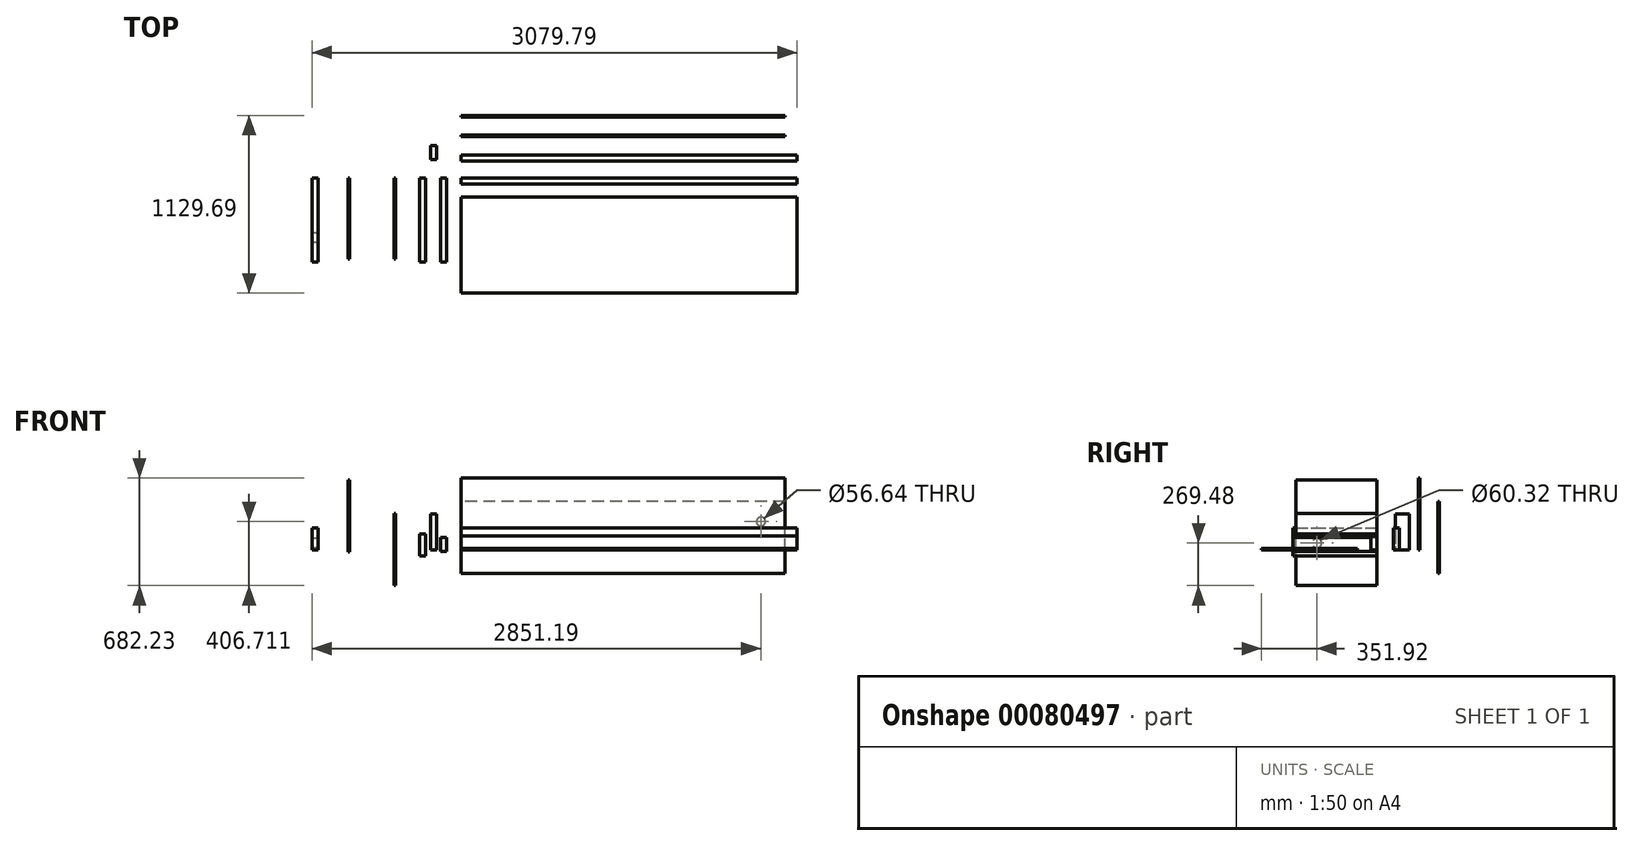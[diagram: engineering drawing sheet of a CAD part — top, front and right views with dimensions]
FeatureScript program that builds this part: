
annotation { "Feature Type Name" : "Feature", "Feature Type Description" : "" }
export const myFeature = defineFeature(function(context is Context, id is Id, definition is map)
    precondition{}
    {
        {
            var Q0;
            Q0=qCreatedBy(makeId("Right.planeOp"),FACE);
            var sketch = newSketch(context, id + "F0", { "sketchPlane" : qUnion([Q0])});
            skLineSegment(sketch, "E0.bottom", {"start": v(0, 0) * mm, "end": v(-38.1, 0) * mm});
            skLineSegment(sketch, "E0.top", {"start": v(0, 88.9) * mm, "end": v(-38.1, 88.9) * mm});
            skLineSegment(sketch, "E0.left", {"start": v(0, 0) * mm, "end": v(0, 88.9) * mm});
            skLineSegment(sketch, "E0.right", {"start": v(-38.1, 0) * mm, "end": v(-38.1, 88.9) * mm});
            skSolve(sketch);
        }
        {
            var Q0;
            Q0=makeQuery(id+"F0.imprint","IMPRINT",FACE,{"disambiguationData":[TD([[makeQuery(id+"F0.imprint","IMPRINT",EDGE,{"derivedFrom":sQuery(id+"F0.wireOp",EDGE,"E0.bottom")}),-1.0]])]});
            extrude(context, id + "F1", {"entities" : qUnion([Q0]), "depth" : 2133.6 * mm});
        }
        {
            var Q0;
            Q0=qCreatedBy(makeId("Front.planeOp"),FACE);
            var sketch = newSketch(context, id + "F2", { "sketchPlane" : qUnion([Q0])});
            skLineSegment(sketch, "E1.bottom", {"start": v(-92.86, -7.97) * mm, "end": v(-130.96, -7.97) * mm});
            skLineSegment(sketch, "E1.top", {"start": v(-92.86, 80.93) * mm, "end": v(-130.96, 80.93) * mm});
            skLineSegment(sketch, "E1.left", {"start": v(-92.86, -7.97) * mm, "end": v(-92.86, 80.93) * mm});
            skLineSegment(sketch, "E1.right", {"start": v(-130.96, -7.97) * mm, "end": v(-130.96, 80.93) * mm});
            skSolve(sketch);
        }
        {
            var Q0;
            Q0=makeQuery(id+"F2.imprint","IMPRINT",FACE,{"disambiguationData":[TD([[makeQuery(id+"F2.imprint","IMPRINT",EDGE,{"derivedFrom":sQuery(id+"F2.wireOp",EDGE,"E1.bottom")}),-1.0]])]});
            extrude(context, id + "F3", {"entities" : qUnion([Q0]), "depth" : 533.4 * mm});
        }
        {
            var Q0;
            Q0=qCreatedBy(makeId("Right.planeOp"),FACE);
            var sketch = newSketch(context, id + "F4", { "sketchPlane" : qUnion([Q0])});
            skLineSegment(sketch, "E2.bottom", {"start": v(105.82, 0) * mm, "end": v(143.92, 0) * mm});
            skLineSegment(sketch, "E2.top", {"start": v(105.82, 139.7) * mm, "end": v(143.92, 139.7) * mm});
            skLineSegment(sketch, "E2.left", {"start": v(105.82, 0) * mm, "end": v(105.82, 139.7) * mm});
            skLineSegment(sketch, "E2.right", {"start": v(143.92, 0) * mm, "end": v(143.92, 139.7) * mm});
            skSolve(sketch);
        }
        {
            var Q0;
            Q0=makeQuery(id+"F4.imprint","IMPRINT",FACE,{"disambiguationData":[TD([[makeQuery(id+"F4.imprint","IMPRINT",EDGE,{"derivedFrom":sQuery(id+"F4.wireOp",EDGE,"E2.bottom")}),1.0]])]});
            extrude(context, id + "F5", {"entities" : qUnion([Q0]), "depth" : 2133.6 * mm});
        }
        {
            var Q0;
            Q0=qCreatedBy(makeId("Front.planeOp"),FACE);
            var sketch = newSketch(context, id + "F6", { "sketchPlane" : qUnion([Q0])});
            skLineSegment(sketch, "E3.bottom", {"start": v(-225.29, -37.86) * mm, "end": v(-263.39, -37.86) * mm});
            skLineSegment(sketch, "E3.top", {"start": v(-225.29, 101.84) * mm, "end": v(-263.39, 101.84) * mm});
            skLineSegment(sketch, "E3.left", {"start": v(-225.29, -37.86) * mm, "end": v(-225.29, 101.84) * mm});
            skLineSegment(sketch, "E3.right", {"start": v(-263.39, -37.86) * mm, "end": v(-263.39, 101.84) * mm});
            skSolve(sketch);
        }
        {
            var Q0;
            Q0=makeQuery(id+"F6.imprint","IMPRINT",FACE,{"disambiguationData":[TD([[makeQuery(id+"F6.imprint","IMPRINT",EDGE,{"derivedFrom":sQuery(id+"F6.wireOp",EDGE,"E3.bottom")}),-1.0]])]});
            extrude(context, id + "F7", {"entities" : qUnion([Q0]), "depth" : 533.4 * mm});
        }
        {
            var Q0;
            Q0=qCreatedBy(makeId("Top.planeOp"),FACE);
            var sketch = newSketch(context, id + "F8", { "sketchPlane" : qUnion([Q0])});
            skLineSegment(sketch, "E4.bottom", {"start": v(-155.43, 116.63) * mm, "end": v(-193.53, 116.63) * mm});
            skLineSegment(sketch, "E4.top", {"start": v(-155.43, 205.53) * mm, "end": v(-193.53, 205.53) * mm});
            skLineSegment(sketch, "E4.left", {"start": v(-155.43, 116.63) * mm, "end": v(-155.43, 205.53) * mm});
            skLineSegment(sketch, "E4.right", {"start": v(-193.53, 116.63) * mm, "end": v(-193.53, 205.53) * mm});
            skSolve(sketch);
        }
        {
            var Q0;
            Q0=makeQuery(id+"F8.imprint","IMPRINT",FACE,{"disambiguationData":[TD([[makeQuery(id+"F8.imprint","IMPRINT",EDGE,{"derivedFrom":sQuery(id+"F8.wireOp",EDGE,"E4.bottom")}),-1.0]])]});
            extrude(context, id + "F9", {"entities" : qUnion([Q0]), "depth" : 228.6 * mm});
        }
        {
            var Q0;
            Q0=qCreatedBy(makeId("Top.planeOp"),FACE);
            var sketch = newSketch(context, id + "F10", { "sketchPlane" : qUnion([Q0])});
            skLineSegment(sketch, "E5.bottom", {"start": v(0, -123.32) * mm, "end": v(2133.6, -123.32) * mm});
            skLineSegment(sketch, "E5.top", {"start": v(0, -732.92) * mm, "end": v(2133.6, -732.92) * mm});
            skLineSegment(sketch, "E5.left", {"start": v(0, -123.32) * mm, "end": v(0, -732.92) * mm});
            skLineSegment(sketch, "E5.right", {"start": v(2133.6, -123.32) * mm, "end": v(2133.6, -732.92) * mm});
            skSolve(sketch);
        }
        {
            var Q0;
            Q0=makeQuery(id+"F10.imprint","IMPRINT",FACE,{"disambiguationData":[TD([[makeQuery(id+"F10.imprint","IMPRINT",EDGE,{"derivedFrom":sQuery(id+"F10.wireOp",EDGE,"E5.bottom")}),-1.0]])]});
            extrude(context, id + "F11", {"entities" : qUnion([Q0]), "depth" : 9.52 * mm});
        }
        {
            var Q0;
            Q0=qCreatedBy(makeId("Right.planeOp"),FACE);
            var sketch = newSketch(context, id + "F12", { "sketchPlane" : qUnion([Q0])});
            skLineSegment(sketch, "E6.bottom", {"start": v(263.25, 0) * mm, "end": v(272.78, 0) * mm});
            skLineSegment(sketch, "E6.top", {"start": v(263.25, 457.2) * mm, "end": v(272.78, 457.2) * mm});
            skLineSegment(sketch, "E6.left", {"start": v(263.25, 0) * mm, "end": v(263.25, 457.2) * mm});
            skLineSegment(sketch, "E6.right", {"start": v(272.78, 0) * mm, "end": v(272.78, 457.2) * mm});
            skSolve(sketch);
        }
        {
            var Q0;
            Q0=makeQuery(id+"F12.imprint","IMPRINT",FACE,{"disambiguationData":[TD([[makeQuery(id+"F12.imprint","IMPRINT",EDGE,{"derivedFrom":sQuery(id+"F12.wireOp",EDGE,"E6.bottom")}),1.0]])]});
            extrude(context, id + "F13", {"entities" : qUnion([Q0]), "depth" : 2057.4 * mm});
        }
        {
            var Q0;
            Q0=qCreatedBy(makeId("Right.planeOp"),FACE);
            var sketch = newSketch(context, id + "F14", { "sketchPlane" : qUnion([Q0])});
            skLineSegment(sketch, "E7.bottom", {"start": v(387.25, -148.52) * mm, "end": v(396.77, -148.52) * mm});
            skLineSegment(sketch, "E7.top", {"start": v(387.25, 308.68) * mm, "end": v(396.77, 308.68) * mm});
            skLineSegment(sketch, "E7.left", {"start": v(387.25, -148.52) * mm, "end": v(387.25, 308.68) * mm});
            skLineSegment(sketch, "E7.right", {"start": v(396.77, -148.52) * mm, "end": v(396.77, 308.68) * mm});
            skSolve(sketch);
        }
        {
            var Q0;
            Q0=makeQuery(id+"F14.imprint","IMPRINT",FACE,{"disambiguationData":[TD([[makeQuery(id+"F14.imprint","IMPRINT",EDGE,{"derivedFrom":sQuery(id+"F14.wireOp",EDGE,"E7.bottom")}),1.0]])]});
            extrude(context, id + "F15", {"entities" : qUnion([Q0]), "depth" : 2057.4 * mm});
        }
        {
            var Q0;
            Q0=qCreatedBy(makeId("Front.planeOp"),FACE);
            var sketch = newSketch(context, id + "F16", { "sketchPlane" : qUnion([Q0])});
            skLineSegment(sketch, "E8.bottom", {"start": v(-425.21, -225.03) * mm, "end": v(-415.69, -225.03) * mm});
            skLineSegment(sketch, "E8.top", {"start": v(-425.21, 232.17) * mm, "end": v(-415.69, 232.17) * mm});
            skLineSegment(sketch, "E8.left", {"start": v(-425.21, -225.03) * mm, "end": v(-425.21, 232.17) * mm});
            skLineSegment(sketch, "E8.right", {"start": v(-415.69, -225.03) * mm, "end": v(-415.69, 232.17) * mm});
            skSolve(sketch);
        }
        {
            var Q0;
            Q0=makeQuery(id+"F16.imprint","IMPRINT",FACE,{"disambiguationData":[TD([[makeQuery(id+"F16.imprint","IMPRINT",EDGE,{"derivedFrom":sQuery(id+"F16.wireOp",EDGE,"E8.bottom")}),1.0]])]});
            extrude(context, id + "F17", {"entities" : qUnion([Q0]), "depth" : 514.35 * mm});
        }
        {
            var Q0;
            Q0=qCreatedBy(makeId("Front.planeOp"),FACE);
            var sketch = newSketch(context, id + "F18", { "sketchPlane" : qUnion([Q0])});
            skLineSegment(sketch, "E9.bottom", {"start": v(-718.56, -12.2) * mm, "end": v(-709.04, -12.2) * mm});
            skLineSegment(sketch, "E9.top", {"start": v(-718.56, 445) * mm, "end": v(-709.04, 445) * mm});
            skLineSegment(sketch, "E9.left", {"start": v(-718.56, -12.2) * mm, "end": v(-718.56, 445) * mm});
            skLineSegment(sketch, "E9.right", {"start": v(-709.04, -12.2) * mm, "end": v(-709.04, 445) * mm});
            skSolve(sketch);
        }
        {
            var Q0;
            Q0=makeQuery(id+"F18.imprint","IMPRINT",FACE,{"disambiguationData":[TD([[makeQuery(id+"F18.imprint","IMPRINT",EDGE,{"derivedFrom":sQuery(id+"F18.wireOp",EDGE,"E9.bottom")}),1.0]])]});
            extrude(context, id + "F19", {"entities" : qUnion([Q0]), "depth" : 514.35 * mm});
        }
        {
            var Q0;
            Q0=makeQuery(id+"F15.opExtrude","SWEPT_FACE",FACE,{"disambiguationData":[OSD([sQuery(id+"F14.wireOp",EDGE,"E7.right")])]});
            var sketch = newSketch(context, id + "F20", { "sketchPlane" : qUnion([Q0])});
            skCircle(sketch, "E10", {"center": v(-1905, 181.68) * mm, "radius": 28.32 * mm});
            skSolve(sketch);
        }
        {
            var Q0;
            Q0=makeQuery(id+"F20.imprint","IMPRINT",FACE,{"disambiguationData":[TD([[makeQuery(id+"F20.imprint","IMPRINT",EDGE,{"derivedFrom":sQuery(id+"F20.wireOp",EDGE,"E10")}),1.0]])]});
            extrude(context, id + "F21", {"entities" : qUnion([Q0]), "operationType" : NewBodyOperationType.REMOVE, "oppositeDirection" : true, "depth" : 25.4 * mm});
        }
        {
            var Q0;
            Q0=qCreatedBy(makeId("Front.planeOp"),FACE);
            var sketch = newSketch(context, id + "F22", { "sketchPlane" : qUnion([Q0])});
            skLineSegment(sketch, "E11.bottom", {"start": v(-908.1, 0) * mm, "end": v(-946.2, 0) * mm});
            skLineSegment(sketch, "E11.top", {"start": v(-908.1, 139.7) * mm, "end": v(-946.2, 139.7) * mm});
            skLineSegment(sketch, "E11.left", {"start": v(-908.1, 0) * mm, "end": v(-908.1, 139.7) * mm});
            skLineSegment(sketch, "E11.right", {"start": v(-946.2, 0) * mm, "end": v(-946.2, 139.7) * mm});
            skSolve(sketch);
        }
        {
            var Q0;
            Q0=makeQuery(id+"F22.imprint","IMPRINT",FACE,{"disambiguationData":[TD([[makeQuery(id+"F22.imprint","IMPRINT",EDGE,{"derivedFrom":sQuery(id+"F22.wireOp",EDGE,"E11.bottom")}),-1.0]])]});
            extrude(context, id + "F23", {"entities" : qUnion([Q0]), "depth" : 533.4 * mm});
        }
        {
            var Q0;
            Q0=makeQuery(id+"F23.opExtrude","SWEPT_FACE",FACE,{"disambiguationData":[OSD([sQuery(id+"F22.wireOp",EDGE,"E11.right")])]});
            var sketch = newSketch(context, id + "F24", { "sketchPlane" : qUnion([Q0])});
            skCircle(sketch, "E12", {"center": v(381, 44.45) * mm, "radius": 30.16 * mm});
            skSolve(sketch);
        }
        {
            var Q0;
            Q0=makeQuery(id+"F24.imprint","IMPRINT",FACE,{"disambiguationData":[TD([[makeQuery(id+"F24.imprint","IMPRINT",EDGE,{"derivedFrom":sQuery(id+"F24.wireOp",EDGE,"E12")}),1.0]])]});
            extrude(context, id + "F25", {"entities" : qUnion([Q0]), "operationType" : NewBodyOperationType.REMOVE, "oppositeDirection" : true, "depth" : 38.1 * mm});
        }
    });
